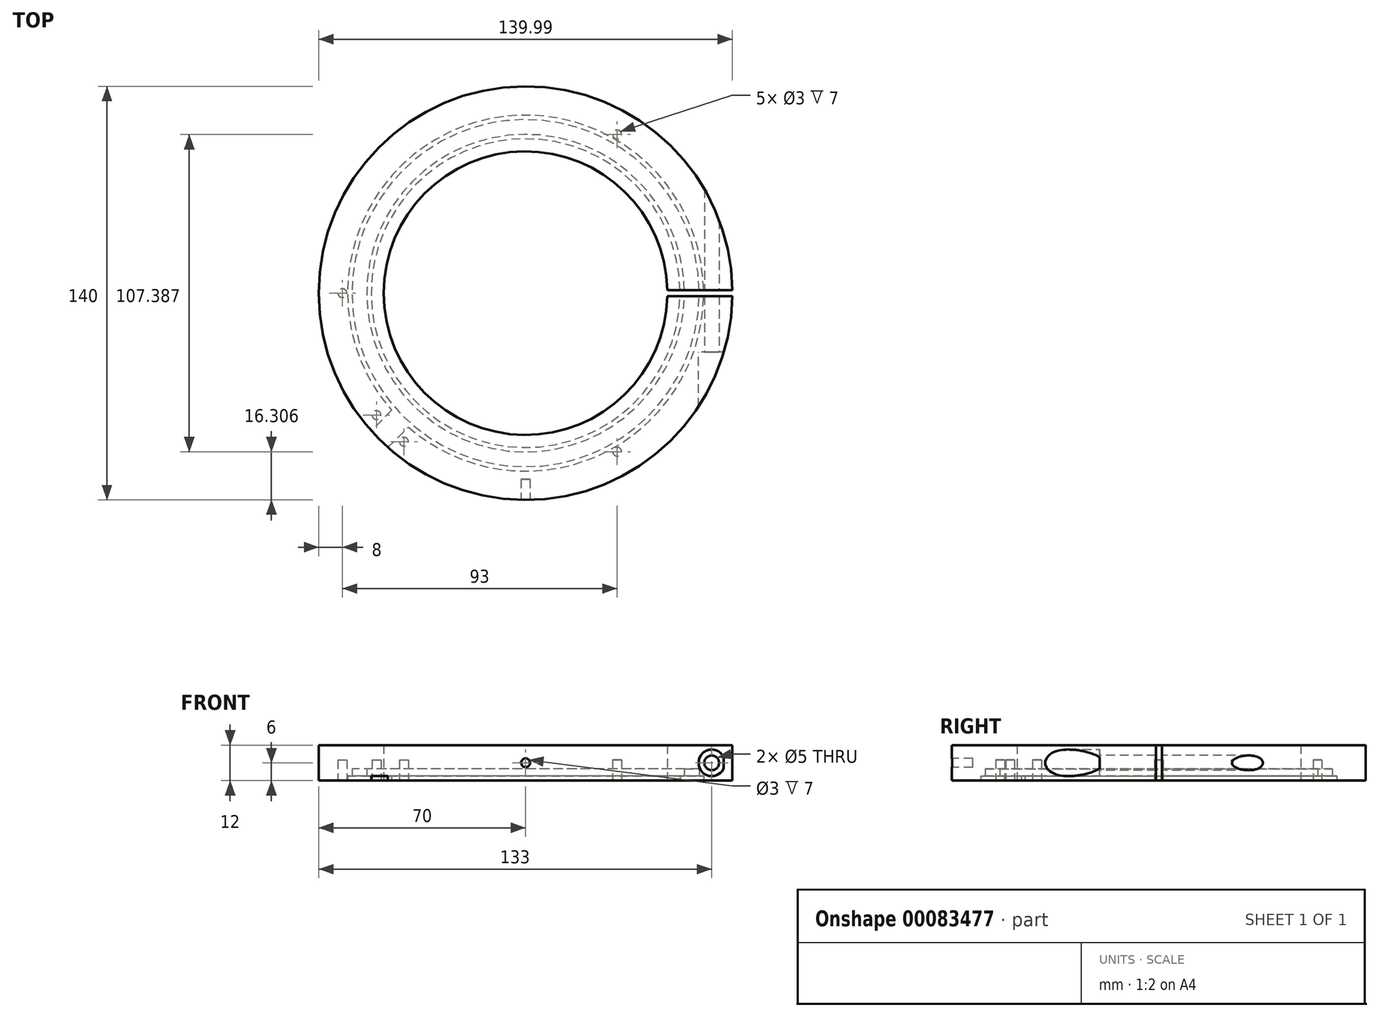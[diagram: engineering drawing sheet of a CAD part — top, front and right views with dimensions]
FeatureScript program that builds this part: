
annotation { "Feature Type Name" : "Feature", "Feature Type Description" : "" }
export const myFeature = defineFeature(function(context is Context, id is Id, definition is map)
    precondition{}
    {
        {
            var Q0;
            Q0=qCreatedBy(makeId("Top.planeOp"),FACE);
            var sketch = newSketch(context, id + "F0", { "sketchPlane" : qUnion([Q0])});
            skArc(sketch, "E0", {"start": v(70, 1) * mm, "mid": v(-70, 0) * mm, "end": v(70, -1) * mm});
            skArc(sketch, "E1", {"start": v(47.99, 1) * mm, "mid": v(-48, 0) * mm, "end": v(47.99, -1) * mm});
            skLineSegment(sketch, "E2", {"start": v(48, 0) * mm, "end": v(70, 0) * mm, "construction": true});
            skPoint(sketch, "E3", {"position": v(59, 0) * mm});
            skLineSegment(sketch, "E4.rect.bottom", {"start": v(70, 1) * mm, "end": v(47.99, 1) * mm});
            skLineSegment(sketch, "E4.rect.top", {"start": v(70, -1) * mm, "end": v(47.99, -1) * mm});
            skPoint(sketch, "E4.rect.left.start.orphan", {"position": v(71.5, 1) * mm});
            skPoint(sketch, "E5.orphan", {"position": v(71.5, -1) * mm});
            skPoint(sketch, "E4.rect.right.start.orphan", {"position": v(46.5, 1) * mm});
            skPoint(sketch, "E6.orphan", {"position": v(46.5, -1) * mm});
            skSolve(sketch);
        }
        {
            var Q0;
            Q0=qSketchRegion(id+"F0",true);
            extrude(context, id + "F1", {"entities" : qUnion([Q0]), "endBound" : BoundingType.SYMMETRIC, "depth" : 12 * mm});
        }
        {
            var Q0;
            Q0=qCreatedBy(makeId("Front.planeOp"),FACE);
            var sketch = newSketch(context, id + "F2", { "sketchPlane" : qUnion([Q0])});
            skCircle(sketch, "E7", {"center": v(63, 0) * mm, "radius": 2.5 * mm});
            skSolve(sketch);
        }
        {
            var Q0;
            Q0=qSketchRegion(id+"F2",true);
            extrude(context, id + "F3", {"entities" : qUnion([Q0]), "operationType" : NewBodyOperationType.REMOVE, "endBound" : BoundingType.SYMMETRIC, "oppositeDirection" : true, "depth" : 83.16 * mm});
        }
        {
            var Q0;
            Q0=qCreatedBy(makeId("Front.planeOp"),FACE);
            cPlane(context, id + "F4", {"entities" : qUnion([Q0]), "cplaneType" : CPlaneType.OFFSET, "offset" : 20 * mm, "width" : 152.4 * mm, "height" : 152.4 * mm});
        }
        {
            var Q0;
            Q0=qCreatedBy(id+"F4.planeOp",FACE);
            var sketch = newSketch(context, id + "F5", { "sketchPlane" : qUnion([Q0])});
            skCircle(sketch, "E8", {"center": v(63, 0) * mm, "radius": 4.5 * mm});
            skSolve(sketch);
        }
        {
            var Q0;
            Q0=qSketchRegion(id+"F5",true);
            var Q1;
            Q1=makeQuery(id+"F1.opExtrude","SWEPT_FACE",FACE,{"disambiguationData":[OSD([sQuery(id+"F0.wireOp",EDGE,"E0")])]});
            extrude(context, id + "F6", {"entities" : qUnion([Q0]), "operationType" : NewBodyOperationType.REMOVE, "endBound" : BoundingType.UP_TO_SURFACE, "endBoundEntityFace" : qUnion([Q1]), "depth" : 25.4 * mm});
        }
        {
            var Q0;
            Q0=makeQuery(id+"F1.opExtrude","CAP_FACE",FACE,{"disambiguationData":[OSD([sQuery(id+"F0.wireOp",EDGE,"E0"),sQuery(id+"F0.wireOp",EDGE,"E1"),sQuery(id+"F0.wireOp",EDGE,"E4.rect.bottom"),sQuery(id+"F0.wireOp",EDGE,"E4.rect.top")])],"isStart":true});
            var sketch = newSketch(context, id + "F7", { "sketchPlane" : qUnion([Q0])});
            skCircle(sketch, "E9", {"center": v(0, 0) * mm, "radius": 60.25 * mm});
            skCircle(sketch, "E10", {"center": v(0, 0) * mm, "radius": 52.25 * mm});
            skSolve(sketch);
        }
        {
            var Q0;
            {var subQ3=sQuery(id+"F7.wireOp",EDGE,"E9");var subQ5=makeQuery(id+"F1.opExtrude","CAP_EDGE",EDGE,{"disambiguationData":[OSD([sQuery(id+"F0.wireOp",EDGE,"E4.rect.bottom")])],"isStart":true});var subQ7=makeQuery(id+"F7.imprint","INTERSECT",VERTEX,{"derivedFrom":[subQ5,subQ3]});Q0=makeQuery(id+"F7.imprint","IMPRINT",FACE,{"disambiguationData":[TD([[makeQuery(id+"F7.imprint","IMPRINT",EDGE,{"disambiguationData":[TD([[subQ7,-1.0]])],"derivedFrom":subQ3}),1.0]])]});}
            var Q1;
            {var subQ3=makeQuery(id+"F1.opExtrude","CAP_EDGE",EDGE,{"disambiguationData":[OSD([sQuery(id+"F0.wireOp",EDGE,"E1")])],"isStart":true});Q1=makeQuery(id+"F7.imprint","IMPRINT",FACE,{"disambiguationData":[TD([[makeQuery(id+"F7.imprint","IMPRINT",EDGE,{"derivedFrom":subQ3}),-1.0]])]});}
            var Q2;
            {var subQ3=sQuery(id+"F7.wireOp",EDGE,"E9");var subQ5=makeQuery(id+"F1.opExtrude","CAP_EDGE",EDGE,{"disambiguationData":[OSD([sQuery(id+"F0.wireOp",EDGE,"E4.rect.bottom")])],"isStart":true});var subQ7=makeQuery(id+"F7.imprint","INTERSECT",VERTEX,{"derivedFrom":[subQ5,subQ3]});Q2=makeQuery(id+"F7.imprint","IMPRINT",FACE,{"disambiguationData":[TD([[makeQuery(id+"F7.imprint","IMPRINT",EDGE,{"disambiguationData":[TD([[subQ7,1.0]])],"derivedFrom":subQ3}),1.0]])]});}
            extrude(context, id + "F8", {"entities" : qUnion([Q0, Q1, Q2]), "operationType" : NewBodyOperationType.REMOVE, "oppositeDirection" : true, "depth" : 1.6 * mm});
        }
        {
            var Q0;
            Q0=makeQuery(id+"F8.boolean.opBoolean","COPY",FACE,{"derivedFrom":makeQuery(id+"F8.opExtrude","CAP_FACE",FACE,{"disambiguationData":[OSD([sQuery(id+"F0.wireOp",EDGE,"E1"),sQuery(id+"F0.wireOp",EDGE,"E4.rect.bottom"),sQuery(id+"F0.wireOp",EDGE,"E4.rect.top"),sQuery(id+"F7.wireOp",EDGE,"E9"),sQuery(id+"F7.wireOp",EDGE,"E10")])],"isStart":false})});
            var sketch = newSketch(context, id + "F9", { "sketchPlane" : qUnion([Q0])});
            skCircle(sketch, "E11", {"center": v(0, 0) * mm, "radius": 58.75 * mm});
            skCircle(sketch, "E12", {"center": v(0, 0) * mm, "radius": 53.75 * mm});
            skSolve(sketch);
        }
        {
            var Q0;
            {var subQ0=sQuery(id+"F0.wireOp",EDGE,"E4.rect.top");var subQ1=sQuery(id+"F0.wireOp",EDGE,"E4.rect.bottom");var subQ2=makeQuery(id+"F8.opExtrude","CAP_FACE",FACE,{"disambiguationData":[OSD([sQuery(id+"F0.wireOp",EDGE,"E1"),subQ1,subQ0,sQuery(id+"F7.wireOp",EDGE,"E9"),sQuery(id+"F7.wireOp",EDGE,"E10")])],"isStart":false});var subQ6=sQuery(id+"F9.wireOp",EDGE,"E11");var subQ8=makeQuery(id+"F8.boolean.opBoolean","INTERSECT",EDGE,{"derivedFrom":[makeQuery(id+"F1.opExtrude","SWEPT_FACE",FACE,{"disambiguationData":[OSD([subQ1])]}),subQ2]});var subQ10=makeQuery(id+"F9.imprint","INTERSECT",VERTEX,{"derivedFrom":[subQ8,subQ6]});Q0=makeQuery(id+"F9.imprint","IMPRINT",FACE,{"disambiguationData":[TD([[makeQuery(id+"F9.imprint","IMPRINT",EDGE,{"disambiguationData":[TD([[subQ10,1.0]])],"derivedFrom":subQ6}),1.0]])]});}
            extrude(context, id + "F10", {"entities" : qUnion([Q0]), "operationType" : NewBodyOperationType.REMOVE, "oppositeDirection" : true, "depth" : 2.4 * mm});
        }
        {
            var Q0;
            {var subQ0=sQuery(id+"F0.wireOp",EDGE,"E0");var subQ1=sQuery(id+"F0.wireOp",EDGE,"E4.rect.bottom");var subQ2=sQuery(id+"F0.wireOp",EDGE,"E4.rect.top");Q0=makeQuery(id+"F8.boolean.opBoolean","SPLIT",FACE,{"disambiguationData":[TD([makeQuery(id+"F1.opExtrude","SWEPT_FACE",FACE,{"disambiguationData":[OSD([subQ0])]})])],"derivedFrom":makeQuery(id+"F1.opExtrude","CAP_FACE",FACE,{"disambiguationData":[OSD([subQ0,sQuery(id+"F0.wireOp",EDGE,"E1"),subQ1,subQ2])],"isStart":true})});}
            var sketch = newSketch(context, id + "F11", { "sketchPlane" : qUnion([Q0])});
            skLineSegment(sketch, "E13", {"start": v(0, 0) * mm, "end": v(-62, 0) * mm, "construction": true});
            skCircle(sketch, "E14", {"center": v(-62, 0) * mm, "radius": 1.5 * mm});
            skSolve(sketch);
        }
        {
            var Q0;
            Q0=qSketchRegion(id+"F11",true);
            extrude(context, id + "F12", {"entities" : qUnion([Q0]), "operationType" : NewBodyOperationType.REMOVE, "oppositeDirection" : true, "depth" : 7 * mm});
        }
        {
            var Q0;
            Q0=makeQuery(id+"F12.boolean.opBoolean","COPY",FACE,{"derivedFrom":makeQuery(id+"F12.opExtrude","SWEPT_FACE",FACE,{"disambiguationData":[OSD([sQuery(id+"F11.wireOp",EDGE,"E14")])]})});
            var Q1;
            Q1=makeQuery(id+"F12.boolean.opBoolean","COPY",FACE,{"derivedFrom":makeQuery(id+"F12.opExtrude","CAP_FACE",FACE,{"disambiguationData":[OSD([sQuery(id+"F11.wireOp",EDGE,"E14")])],"isStart":false})});
            var Q2;
            Q2=makeQuery(id+"F1.opExtrude","SWEPT_FACE",FACE,{"disambiguationData":[OSD([sQuery(id+"F0.wireOp",EDGE,"E1")])]});
            circularPattern(context, id + "F13", {"faces" : qUnion([Q0, Q1]), "axis" : qUnion([Q2]), "angle" : 120 * degree, "instanceCount" : 3, "patternType" : PatternType.FACE});
        }
        {
            var Q0;
            Q0=qCreatedBy(makeId("Top.planeOp"),FACE);
            var sketch = newSketch(context, id + "F14", { "sketchPlane" : qUnion([Q0])});
            skLineSegment(sketch, "E15", {"start": v(0, 0) * mm, "end": v(-49.5, -49.5) * mm, "construction": true});
            skSolve(sketch);
        }
        {
            var Q0;
            {var subQ0=sQuery(id+"F0.wireOp",EDGE,"E0");var subQ1=sQuery(id+"F0.wireOp",EDGE,"E4.rect.bottom");var subQ2=sQuery(id+"F0.wireOp",EDGE,"E4.rect.top");Q0=makeQuery(id+"F8.boolean.opBoolean","SPLIT",FACE,{"disambiguationData":[TD([makeQuery(id+"F1.opExtrude","SWEPT_FACE",FACE,{"disambiguationData":[OSD([subQ0])]})])],"derivedFrom":makeQuery(id+"F1.opExtrude","CAP_FACE",FACE,{"disambiguationData":[OSD([subQ0,sQuery(id+"F0.wireOp",EDGE,"E1"),subQ1,subQ2])],"isStart":true})});}
            var sketch = newSketch(context, id + "F15", { "sketchPlane" : qUnion([Q0])});
            skLineSegment(sketch, "E16", {"start": v(-48.17, 53.82) * mm, "end": v(-39.68, 45.34) * mm});
            skLineSegment(sketch, "E17", {"start": v(-39.68, 45.34) * mm, "end": v(-45.34, 39.68) * mm});
            skLineSegment(sketch, "E18", {"start": v(-45.34, 39.68) * mm, "end": v(-53.82, 48.17) * mm});
            skLineSegment(sketch, "E19", {"start": v(-48.17, 53.82) * mm, "end": v(-53.82, 48.17) * mm});
            skSolve(sketch);
        }
        {
            var Q0;
            Q0=qSketchRegion(id+"F15",true);
            extrude(context, id + "F16", {"entities" : qUnion([Q0]), "operationType" : NewBodyOperationType.REMOVE, "oppositeDirection" : true, "depth" : 1.6 * mm});
        }
        {
            var Q0;
            {var subQ0=sQuery(id+"F0.wireOp",EDGE,"E0");var subQ1=sQuery(id+"F0.wireOp",EDGE,"E4.rect.bottom");var subQ2=sQuery(id+"F0.wireOp",EDGE,"E4.rect.top");var subQ4=makeQuery(id+"F1.opExtrude","SWEPT_FACE",FACE,{"disambiguationData":[OSD([subQ1])]});var subQ5=makeQuery(id+"F1.opExtrude","SWEPT_FACE",FACE,{"disambiguationData":[OSD([subQ0])]});Q0=makeQuery(id+"F16.boolean.opBoolean","SPLIT",FACE,{"disambiguationData":[TD([subQ4])],"derivedFrom":makeQuery(id+"F8.boolean.opBoolean","SPLIT",FACE,{"disambiguationData":[TD([subQ5])],"derivedFrom":makeQuery(id+"F1.opExtrude","CAP_FACE",FACE,{"disambiguationData":[OSD([subQ0,sQuery(id+"F0.wireOp",EDGE,"E1"),subQ1,subQ2])],"isStart":true})})});}
            var sketch = newSketch(context, id + "F17", { "sketchPlane" : qUnion([Q0])});
            skCircle(sketch, "E20", {"center": v(-50.46, 41.26) * mm, "radius": 1.5 * mm});
            skCircle(sketch, "E21", {"center": v(-41.14, 50.33) * mm, "radius": 1.5 * mm});
            skCircle(sketch, "E22", {"center": v(0, -1.28) * mm, "radius": 66 * mm, "construction": true});
            skSolve(sketch);
        }
        {
            var Q0;
            Q0=qSketchRegion(id+"F17",true);
            extrude(context, id + "F18", {"entities" : qUnion([Q0]), "operationType" : NewBodyOperationType.REMOVE, "oppositeDirection" : true, "depth" : 7 * mm});
        }
        {
            var Q0;
            Q0=qCreatedBy(makeId("Front.planeOp"),FACE);
            cPlane(context, id + "F19", {"entities" : qUnion([Q0]), "cplaneType" : CPlaneType.OFFSET, "offset" : 70 * mm, "width" : 150 * mm, "height" : 150 * mm});
        }
        {
            var Q0;
            Q0=qCreatedBy(id+"F19.planeOp",FACE);
            var sketch = newSketch(context, id + "F20", { "sketchPlane" : qUnion([Q0])});
            skCircle(sketch, "E23", {"center": v(0, 0) * mm, "radius": 1.5 * mm});
            skSolve(sketch);
        }
        {
            var Q0;
            Q0=qSketchRegion(id+"F20",true);
            extrude(context, id + "F21", {"entities" : qUnion([Q0]), "operationType" : NewBodyOperationType.REMOVE, "oppositeDirection" : true, "depth" : 7 * mm});
        }
    });
